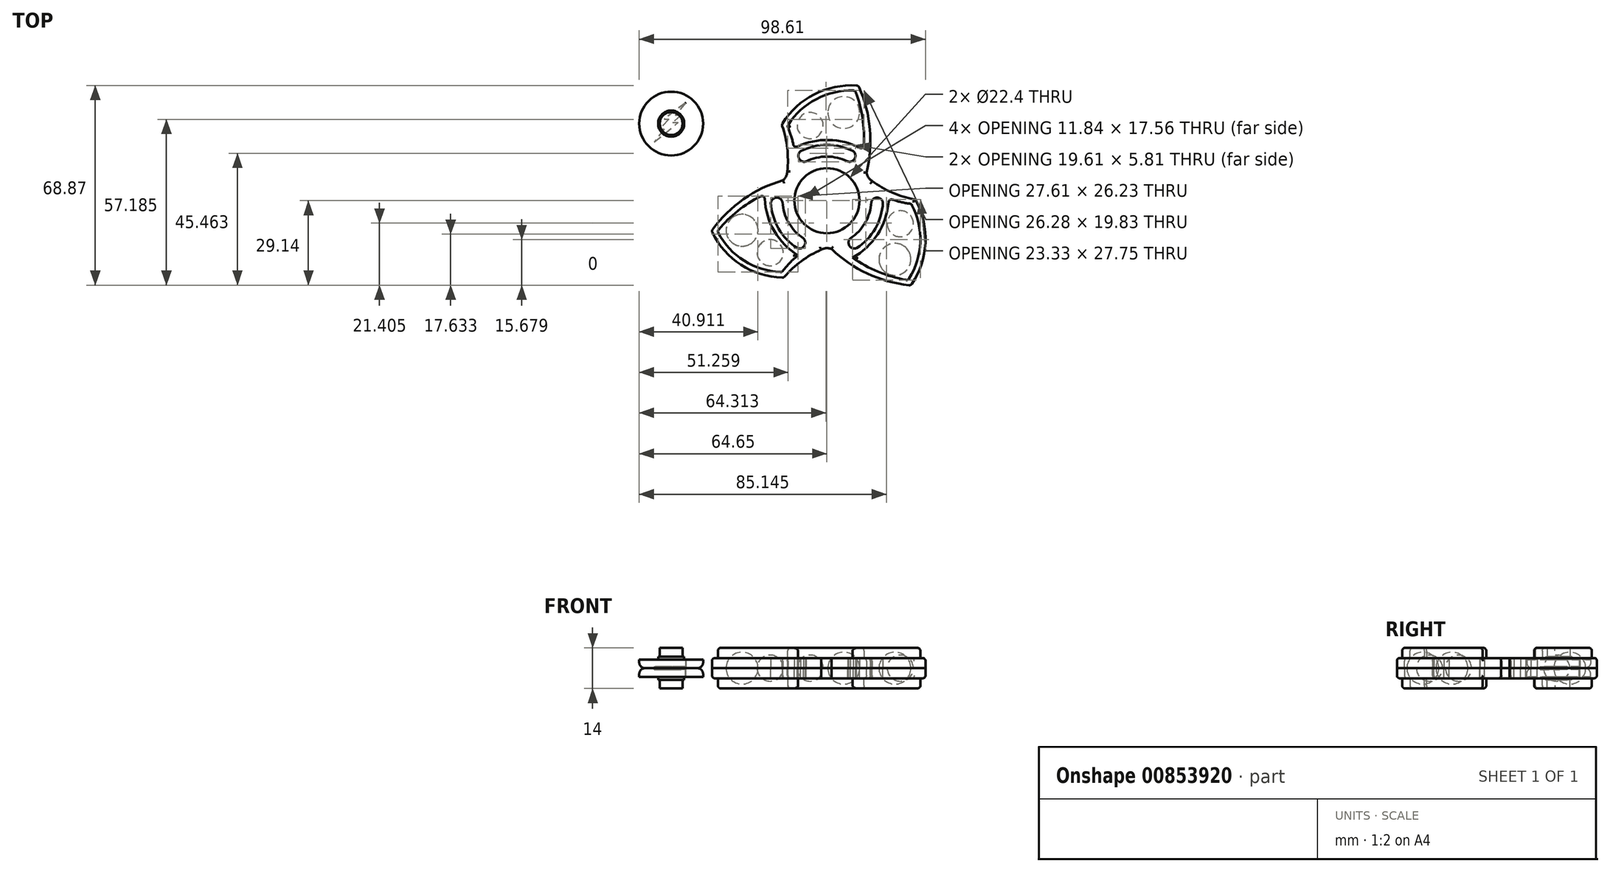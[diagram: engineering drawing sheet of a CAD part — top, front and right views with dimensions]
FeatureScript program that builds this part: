
annotation { "Feature Type Name" : "Feature", "Feature Type Description" : "" }
export const myFeature = defineFeature(function(context is Context, id is Id, definition is map)
    precondition{}
    {
        {
            var Q0;
            Q0=qCreatedBy(makeId("Top.planeOp"),FACE);
            var sketch = newSketch(context, id + "F0", { "sketchPlane" : qUnion([Q0])});
            skCircle(sketch, "E0", {"center": v(0, 0) * mm, "radius": 13.7 * mm});
            skCircle(sketch, "E1", {"center": v(0, 0) * mm, "radius": 11.2 * mm});
            skCircle(sketch, "E2", {"center": v(-53.65, 26.57) * mm, "radius": 11 * mm});
            skCircle(sketch, "E3", {"center": v(-53.65, 26.57) * mm, "radius": 3.95 * mm});
            skCircle(sketch, "E4", {"center": v(-53.65, 26.57) * mm, "radius": 6.92 * mm});
            skCircle(sketch, "E5", {"center": v(-53.65, 26.57) * mm, "radius": 8.68 * mm});
            skPoint(sketch, "E6.MirrorP", {"position": v(9.06, 17.07) * mm});
            skPoint(sketch, "E7.MirrorP", {"position": v(7.21, 13.5) * mm});
            skPoint(sketch, "E8", {"position": v(0, 15.2) * mm});
            skPoint(sketch, "E9", {"position": v(0, 19.23) * mm});
            skArc(sketch, "E10", {"start": v(7.21, 13.5) * mm, "mid": v(0, 15.2) * mm, "end": v(-7.21, 13.5) * mm});
            skArc(sketch, "E11", {"start": v(9.06, 17.07) * mm, "mid": v(0, 19.23) * mm, "end": v(-9.06, 17.07) * mm});
            skArc(sketch, "E12", {"start": v(-9.06, 17.07) * mm, "mid": v(-9.6, 14.52) * mm, "end": v(-7.21, 13.5) * mm});
            skArc(sketch, "E13.MirrorCS", {"start": v(9.06, 17.07) * mm, "mid": v(9.6, 14.52) * mm, "end": v(7.21, 13.5) * mm});
            skPoint(sketch, "E14", {"position": v(0, 20.93) * mm});
            skArc(sketch, "E15", {"start": v(12.63, 17.5) * mm, "mid": v(0.7, 20.92) * mm, "end": v(-11.37, 18.03) * mm});
            skCircle(sketch, "E16.MirrorC", {"center": v(-5.77, 25.88) * mm, "radius": 4.5 * mm});
            skLineSegment(sketch, "E17", {"start": v(0.3, 30.4) * mm, "end": v(11.3, 30.4) * mm});
            skCircle(sketch, "E18", {"center": v(5.8, 30.4) * mm, "radius": 5.5 * mm});
            skLineSegment(sketch, "E19", {"start": v(-1.27, 25.88) * mm, "end": v(-10.27, 25.88) * mm});
            skArc(sketch, "E20", {"start": v(-11.37, 18.03) * mm, "mid": v(-12.22, 21.95) * mm, "end": v(-13.6, 25.71) * mm});
            skArc(sketch, "E21", {"start": v(12.63, 17.5) * mm, "mid": v(12.36, 27.87) * mm, "end": v(9.77, 37.93) * mm});
            skArc(sketch, "E22", {"start": v(9.77, 37.93) * mm, "mid": v(-3.6, 35.05) * mm, "end": v(-13.6, 25.71) * mm});
            skPoint(sketch, "E23", {"position": v(12.8, 22.5) * mm});
            skPoint(sketch, "E24", {"position": v(-15.55, 26.2) * mm});
            skPoint(sketch, "E25", {"position": v(10.84, 39.63) * mm});
            skPoint(sketch, "E26", {"position": v(13.64, 9.66) * mm});
            skPoint(sketch, "E27", {"position": v(-13.65, 10.14) * mm});
            skArc(sketch, "E28", {"start": v(10.84, 39.63) * mm, "mid": v(-4.28, 36.7) * mm, "end": v(-15.55, 26.2) * mm});
            skArc(sketch, "E29", {"start": v(13.64, 9.66) * mm, "mid": v(14.79, 24.88) * mm, "end": v(10.84, 39.63) * mm});
            skPoint(sketch, "E30", {"position": v(14.97, 19.42) * mm});
            skPoint(sketch, "E31", {"position": v(14.46, 27.55) * mm});
            skArc(sketch, "E32", {"start": v(-13.65, 10.14) * mm, "mid": v(-13.69, 18.28) * mm, "end": v(-15.55, 26.2) * mm});
            skPoint(sketch, "E33.1.0", {"position": v(-13.16, -7.6) * mm});
            skArc(sketch, "E33.1.1", {"start": v(-21.47, 2.2) * mm, "mid": v(-18.47, -9.85) * mm, "end": v(-9.93, -18.86) * mm});
            skCircle(sketch, "E33.1.2", {"center": v(-29.22, -10.18) * mm, "radius": 5.5 * mm});
            skArc(sketch, "E33.1.3", {"start": v(-19.31, -0.69) * mm, "mid": v(-16.65, -9.61) * mm, "end": v(-10.25, -16.38) * mm});
            skArc(sketch, "E33.1.4", {"start": v(-15.29, -0.5) * mm, "mid": v(-13.16, -7.6) * mm, "end": v(-8.08, -13) * mm});
            skPoint(sketch, "E33.1.5", {"position": v(-25.89, -0.17) * mm});
            skArc(sketch, "E33.1.6", {"start": v(-21.47, 2.2) * mm, "mid": v(-30.32, -3.23) * mm, "end": v(-37.74, -10.5) * mm});
            skLineSegment(sketch, "E33.1.7", {"start": v(-26.47, -14.95) * mm, "end": v(-31.97, -5.42) * mm});
            skPoint(sketch, "E33.1.8", {"position": v(-16.65, -9.61) * mm});
            skPoint(sketch, "E33.1.9", {"position": v(-15.29, -0.5) * mm});
            skPoint(sketch, "E33.1.10", {"position": v(-18.12, -10.46) * mm});
            skArc(sketch, "E33.1.11", {"start": v(-9.93, -18.86) * mm, "mid": v(-12.9, -21.56) * mm, "end": v(-15.46, -24.64) * mm});
            skPoint(sketch, "E33.1.12", {"position": v(-39.74, -10.43) * mm});
            skPoint(sketch, "E33.1.13", {"position": v(-24.3, 3.25) * mm});
            skPoint(sketch, "E33.1.14", {"position": v(-14.92, -26.57) * mm});
            skPoint(sketch, "E33.1.15", {"position": v(-15.19, 6.98) * mm});
            skPoint(sketch, "E33.1.16", {"position": v(-19.31, -0.69) * mm});
            skLineSegment(sketch, "E33.1.17", {"start": v(-21.78, -14.04) * mm, "end": v(-17.28, -21.83) * mm});
            skPoint(sketch, "E33.1.18", {"position": v(-31.1, -1.26) * mm});
            skArc(sketch, "E33.1.19", {"start": v(-39.74, -10.43) * mm, "mid": v(-29.64, -22.06) * mm, "end": v(-14.92, -26.57) * mm});
            skArc(sketch, "E33.1.20", {"start": v(-19.31, -0.69) * mm, "mid": v(-17.38, 1.05) * mm, "end": v(-15.29, -0.5) * mm});
            skArc(sketch, "E33.1.21", {"start": v(-37.74, -10.5) * mm, "mid": v(-28.55, -20.65) * mm, "end": v(-15.46, -24.64) * mm});
            skArc(sketch, "E33.1.22", {"start": v(-10.25, -16.38) * mm, "mid": v(-7.78, -15.57) * mm, "end": v(-8.08, -13) * mm});
            skCircle(sketch, "E33.1.23", {"center": v(-19.53, -17.93) * mm, "radius": 4.5 * mm});
            skArc(sketch, "E33.1.24", {"start": v(-15.19, 6.98) * mm, "mid": v(-28.94, 0.36) * mm, "end": v(-39.74, -10.43) * mm});
            skArc(sketch, "E33.1.25", {"start": v(-1.96, -16.89) * mm, "mid": v(-8.99, -21) * mm, "end": v(-14.92, -26.57) * mm});
            skPoint(sketch, "E33.2.0", {"position": v(13.16, -7.6) * mm});
            skArc(sketch, "E33.2.1", {"start": v(8.83, -19.69) * mm, "mid": v(17.77, -11.07) * mm, "end": v(21.3, 0.83) * mm});
            skCircle(sketch, "E33.2.2", {"center": v(23.43, -20.21) * mm, "radius": 5.5 * mm});
            skArc(sketch, "E33.2.3", {"start": v(10.25, -16.38) * mm, "mid": v(16.65, -9.61) * mm, "end": v(19.31, -0.69) * mm});
            skArc(sketch, "E33.2.4", {"start": v(8.08, -13) * mm, "mid": v(13.16, -7.6) * mm, "end": v(15.29, -0.5) * mm});
            skPoint(sketch, "E33.2.5", {"position": v(13.1, -22.33) * mm});
            skArc(sketch, "E33.2.6", {"start": v(8.83, -19.69) * mm, "mid": v(17.96, -24.64) * mm, "end": v(27.96, -27.43) * mm});
            skLineSegment(sketch, "E33.2.7", {"start": v(26.18, -15.45) * mm, "end": v(20.68, -24.98) * mm});
            skPoint(sketch, "E33.2.8", {"position": v(16.65, -9.61) * mm});
            skPoint(sketch, "E33.2.9", {"position": v(8.08, -13) * mm});
            skPoint(sketch, "E33.2.10", {"position": v(18.12, -10.46) * mm});
            skArc(sketch, "E33.2.11", {"start": v(21.3, 0.83) * mm, "mid": v(25.12, -0.4) * mm, "end": v(29.07, -1.07) * mm});
            skPoint(sketch, "E33.2.12", {"position": v(28.9, -29.2) * mm});
            skPoint(sketch, "E33.2.13", {"position": v(9.33, -22.67) * mm});
            skPoint(sketch, "E33.2.14", {"position": v(30.47, 0.36) * mm});
            skPoint(sketch, "E33.2.15", {"position": v(1.55, -16.65) * mm});
            skPoint(sketch, "E33.2.16", {"position": v(10.25, -16.38) * mm});
            skLineSegment(sketch, "E33.2.17", {"start": v(23.04, -11.84) * mm, "end": v(27.54, -4.05) * mm});
            skPoint(sketch, "E33.2.18", {"position": v(16.63, -26.3) * mm});
            skArc(sketch, "E33.2.19", {"start": v(28.9, -29.2) * mm, "mid": v(33.92, -14.64) * mm, "end": v(30.47, 0.36) * mm});
            skArc(sketch, "E33.2.20", {"start": v(10.25, -16.38) * mm, "mid": v(7.78, -15.57) * mm, "end": v(8.08, -13) * mm});
            skArc(sketch, "E33.2.21", {"start": v(27.96, -27.43) * mm, "mid": v(32.16, -14.4) * mm, "end": v(29.07, -1.07) * mm});
            skArc(sketch, "E33.2.22", {"start": v(19.31, -0.69) * mm, "mid": v(17.38, 1.05) * mm, "end": v(15.29, -0.5) * mm});
            skCircle(sketch, "E33.2.23", {"center": v(25.3, -7.95) * mm, "radius": 4.5 * mm});
            skArc(sketch, "E33.2.24", {"start": v(1.55, -16.65) * mm, "mid": v(14.16, -25.25) * mm, "end": v(28.9, -29.2) * mm});
            skArc(sketch, "E33.2.25", {"start": v(15.6, 6.75) * mm, "mid": v(22.67, 2.71) * mm, "end": v(30.47, 0.36) * mm});
            skArc(sketch, "E34", {"start": v(-15.19, 6.98) * mm, "mid": v(-14.07, 8.4) * mm, "end": v(-13.65, 10.14) * mm});
            skArc(sketch, "E35.1.0", {"start": v(1.55, -16.65) * mm, "mid": v(-0.23, -16.38) * mm, "end": v(-1.96, -16.89) * mm});
            skArc(sketch, "E35.2.0", {"start": v(13.64, 9.66) * mm, "mid": v(14.3, 7.99) * mm, "end": v(15.6, 6.75) * mm});
            skCircle(sketch, "E36", {"center": v(-53.65, 26.57) * mm, "radius": 4.5 * mm});
            skLineSegment(sketch, "E37", {"start": v(-48.56, 33.87) * mm, "end": v(-56.1, 28.05) * mm});
            skLineSegment(sketch, "E38", {"start": v(-56.1, 28.05) * mm, "end": v(-54.44, 28.05) * mm});
            skLineSegment(sketch, "E39", {"start": v(-54.44, 28.05) * mm, "end": v(-57.71, 24.64) * mm});
            skLineSegment(sketch, "E40", {"start": v(-57.71, 24.64) * mm, "end": v(-56.1, 24.64) * mm});
            skLineSegment(sketch, "E41", {"start": v(-56.1, 24.64) * mm, "end": v(-59.52, 20.18) * mm});
            skLineSegment(sketch, "E42", {"start": v(-59.52, 20.18) * mm, "end": v(-51.2, 26.98) * mm});
            skLineSegment(sketch, "E43", {"start": v(-48.56, 33.87) * mm, "end": v(-52.2, 29.55) * mm});
            skLineSegment(sketch, "E44", {"start": v(-52.2, 29.55) * mm, "end": v(-50.27, 29.55) * mm});
            skLineSegment(sketch, "E45", {"start": v(-50.27, 29.55) * mm, "end": v(-53.14, 26.91) * mm});
            skLineSegment(sketch, "E46", {"start": v(-53.14, 26.91) * mm, "end": v(-51.2, 26.98) * mm});
            skSolve(sketch);
        }
        {
            var Q0;
            Q0=makeQuery(id+"F0.imprint","IMPRINT",FACE,{"disambiguationData":[TD([[makeQuery(id+"F0.imprint","IMPRINT",EDGE,{"derivedFrom":sQuery(id+"F0.wireOp",EDGE,"E0")}),-1.0]])]});
            var Q1;
            Q1=makeQuery(id+"F0.imprint","IMPRINT",FACE,{"disambiguationData":[TD([[makeQuery(id+"F0.imprint","IMPRINT",EDGE,{"derivedFrom":sQuery(id+"F0.wireOp",EDGE,"E33.2.1")}),-1.0]])]});
            var Q2;
            {var subQ0=sQuery(id+"F0.wireOp",EDGE,"E33.2.17");Q2=makeQuery(id+"F0.imprint","IMPRINT",FACE,{"disambiguationData":[TD([[makeQuery(id+"F0.imprint","IMPRINT",EDGE,{"derivedFrom":subQ0}),-1.0]])]});}
            var Q3;
            {var subQ0=sQuery(id+"F0.wireOp",EDGE,"E33.2.17");Q3=makeQuery(id+"F0.imprint","IMPRINT",FACE,{"disambiguationData":[TD([[makeQuery(id+"F0.imprint","IMPRINT",EDGE,{"derivedFrom":subQ0}),1.0]])]});}
            var Q4;
            {var subQ0=sQuery(id+"F0.wireOp",EDGE,"E33.2.7");Q4=makeQuery(id+"F0.imprint","IMPRINT",FACE,{"disambiguationData":[TD([[makeQuery(id+"F0.imprint","IMPRINT",EDGE,{"derivedFrom":subQ0}),-1.0]])]});}
            var Q5;
            {var subQ0=sQuery(id+"F0.wireOp",EDGE,"E33.2.7");Q5=makeQuery(id+"F0.imprint","IMPRINT",FACE,{"disambiguationData":[TD([[makeQuery(id+"F0.imprint","IMPRINT",EDGE,{"derivedFrom":subQ0}),1.0]])]});}
            var Q6;
            Q6=makeQuery(id+"F0.imprint","IMPRINT",FACE,{"disambiguationData":[TD([[makeQuery(id+"F0.imprint","IMPRINT",EDGE,{"derivedFrom":sQuery(id+"F0.wireOp",EDGE,"E33.1.1")}),-1.0]])]});
            var Q7;
            {var subQ0=sQuery(id+"F0.wireOp",EDGE,"E33.1.17");Q7=makeQuery(id+"F0.imprint","IMPRINT",FACE,{"disambiguationData":[TD([[makeQuery(id+"F0.imprint","IMPRINT",EDGE,{"derivedFrom":subQ0}),1.0]])]});}
            var Q8;
            {var subQ0=sQuery(id+"F0.wireOp",EDGE,"E33.1.17");Q8=makeQuery(id+"F0.imprint","IMPRINT",FACE,{"disambiguationData":[TD([[makeQuery(id+"F0.imprint","IMPRINT",EDGE,{"derivedFrom":subQ0}),-1.0]])]});}
            var Q9;
            {var subQ0=sQuery(id+"F0.wireOp",EDGE,"E33.1.7");Q9=makeQuery(id+"F0.imprint","IMPRINT",FACE,{"disambiguationData":[TD([[makeQuery(id+"F0.imprint","IMPRINT",EDGE,{"derivedFrom":subQ0}),-1.0]])]});}
            var Q10;
            {var subQ0=sQuery(id+"F0.wireOp",EDGE,"E33.1.7");Q10=makeQuery(id+"F0.imprint","IMPRINT",FACE,{"disambiguationData":[TD([[makeQuery(id+"F0.imprint","IMPRINT",EDGE,{"derivedFrom":subQ0}),1.0]])]});}
            var Q11;
            Q11=makeQuery(id+"F0.imprint","IMPRINT",FACE,{"disambiguationData":[TD([[makeQuery(id+"F0.imprint","IMPRINT",EDGE,{"derivedFrom":sQuery(id+"F0.wireOp",EDGE,"E15")}),-1.0]])]});
            var Q12;
            {var subQ0=sQuery(id+"F0.wireOp",EDGE,"E17");Q12=makeQuery(id+"F0.imprint","IMPRINT",FACE,{"disambiguationData":[TD([[makeQuery(id+"F0.imprint","IMPRINT",EDGE,{"derivedFrom":subQ0}),-1.0]])]});}
            var Q13;
            {var subQ0=sQuery(id+"F0.wireOp",EDGE,"E17");Q13=makeQuery(id+"F0.imprint","IMPRINT",FACE,{"disambiguationData":[TD([[makeQuery(id+"F0.imprint","IMPRINT",EDGE,{"derivedFrom":subQ0}),1.0]])]});}
            var Q14;
            {var subQ0=sQuery(id+"F0.wireOp",EDGE,"E19");Q14=makeQuery(id+"F0.imprint","IMPRINT",FACE,{"disambiguationData":[TD([[makeQuery(id+"F0.imprint","IMPRINT",EDGE,{"derivedFrom":subQ0}),-1.0]])]});}
            var Q15;
            {var subQ0=sQuery(id+"F0.wireOp",EDGE,"E19");Q15=makeQuery(id+"F0.imprint","IMPRINT",FACE,{"disambiguationData":[TD([[makeQuery(id+"F0.imprint","IMPRINT",EDGE,{"derivedFrom":subQ0}),1.0]])]});}
            var Q16;
            Q16=makeQuery(id+"F0.imprint","IMPRINT",FACE,{"disambiguationData":[TD([[makeQuery(id+"F0.imprint","IMPRINT",EDGE,{"derivedFrom":sQuery(id+"F0.wireOp",EDGE,"E0")}),1.0]])]});
            extrude(context, id + "F1", {"entities" : qUnion([Q0, Q1, Q2, Q3, Q4, Q5, Q6, Q7, Q8, Q9, Q10, Q11, Q12, Q13, Q14, Q15, Q16]), "depth" : 3.5 * mm, "offsetDistance" : 25 * mm});
        }
        {
            var Q0;
            Q0=makeQuery(id+"F0.imprint","IMPRINT",FACE,{"disambiguationData":[TD([[makeQuery(id+"F0.imprint","IMPRINT",EDGE,{"derivedFrom":sQuery(id+"F0.wireOp",EDGE,"E15")}),-1.0]])]});
            var Q1;
            Q1=makeQuery(id+"F0.imprint","IMPRINT",FACE,{"disambiguationData":[TD([[makeQuery(id+"F0.imprint","IMPRINT",EDGE,{"derivedFrom":sQuery(id+"F0.wireOp",EDGE,"E33.1.1")}),-1.0]])]});
            var Q2;
            Q2=makeQuery(id+"F0.imprint","IMPRINT",FACE,{"disambiguationData":[TD([[makeQuery(id+"F0.imprint","IMPRINT",EDGE,{"derivedFrom":sQuery(id+"F0.wireOp",EDGE,"E33.2.1")}),-1.0]])]});
            var Q3;
            {var subQ0=sQuery(id+"F0.wireOp",EDGE,"E33.1.7");Q3=makeQuery(id+"F0.imprint","IMPRINT",FACE,{"disambiguationData":[TD([[makeQuery(id+"F0.imprint","IMPRINT",EDGE,{"derivedFrom":subQ0}),1.0]])]});}
            var Q4;
            {var subQ0=sQuery(id+"F0.wireOp",EDGE,"E33.1.7");Q4=makeQuery(id+"F0.imprint","IMPRINT",FACE,{"disambiguationData":[TD([[makeQuery(id+"F0.imprint","IMPRINT",EDGE,{"derivedFrom":subQ0}),-1.0]])]});}
            var Q5;
            {var subQ0=sQuery(id+"F0.wireOp",EDGE,"E33.1.17");Q5=makeQuery(id+"F0.imprint","IMPRINT",FACE,{"disambiguationData":[TD([[makeQuery(id+"F0.imprint","IMPRINT",EDGE,{"derivedFrom":subQ0}),-1.0]])]});}
            var Q6;
            {var subQ0=sQuery(id+"F0.wireOp",EDGE,"E33.1.17");Q6=makeQuery(id+"F0.imprint","IMPRINT",FACE,{"disambiguationData":[TD([[makeQuery(id+"F0.imprint","IMPRINT",EDGE,{"derivedFrom":subQ0}),1.0]])]});}
            var Q7;
            {var subQ0=sQuery(id+"F0.wireOp",EDGE,"E19");Q7=makeQuery(id+"F0.imprint","IMPRINT",FACE,{"disambiguationData":[TD([[makeQuery(id+"F0.imprint","IMPRINT",EDGE,{"derivedFrom":subQ0}),1.0]])]});}
            var Q8;
            {var subQ0=sQuery(id+"F0.wireOp",EDGE,"E19");Q8=makeQuery(id+"F0.imprint","IMPRINT",FACE,{"disambiguationData":[TD([[makeQuery(id+"F0.imprint","IMPRINT",EDGE,{"derivedFrom":subQ0}),-1.0]])]});}
            var Q9;
            {var subQ0=sQuery(id+"F0.wireOp",EDGE,"E17");Q9=makeQuery(id+"F0.imprint","IMPRINT",FACE,{"disambiguationData":[TD([[makeQuery(id+"F0.imprint","IMPRINT",EDGE,{"derivedFrom":subQ0}),-1.0]])]});}
            var Q10;
            {var subQ0=sQuery(id+"F0.wireOp",EDGE,"E17");Q10=makeQuery(id+"F0.imprint","IMPRINT",FACE,{"disambiguationData":[TD([[makeQuery(id+"F0.imprint","IMPRINT",EDGE,{"derivedFrom":subQ0}),1.0]])]});}
            var Q11;
            {var subQ0=sQuery(id+"F0.wireOp",EDGE,"E33.2.17");Q11=makeQuery(id+"F0.imprint","IMPRINT",FACE,{"disambiguationData":[TD([[makeQuery(id+"F0.imprint","IMPRINT",EDGE,{"derivedFrom":subQ0}),1.0]])]});}
            var Q12;
            {var subQ0=sQuery(id+"F0.wireOp",EDGE,"E33.2.17");Q12=makeQuery(id+"F0.imprint","IMPRINT",FACE,{"disambiguationData":[TD([[makeQuery(id+"F0.imprint","IMPRINT",EDGE,{"derivedFrom":subQ0}),-1.0]])]});}
            var Q13;
            {var subQ0=sQuery(id+"F0.wireOp",EDGE,"E33.2.7");Q13=makeQuery(id+"F0.imprint","IMPRINT",FACE,{"disambiguationData":[TD([[makeQuery(id+"F0.imprint","IMPRINT",EDGE,{"derivedFrom":subQ0}),-1.0]])]});}
            var Q14;
            {var subQ0=sQuery(id+"F0.wireOp",EDGE,"E33.2.7");Q14=makeQuery(id+"F0.imprint","IMPRINT",FACE,{"disambiguationData":[TD([[makeQuery(id+"F0.imprint","IMPRINT",EDGE,{"derivedFrom":subQ0}),1.0]])]});}
            extrude(context, id + "F2", {"entities" : qUnion([Q0, Q1, Q2, Q3, Q4, Q5, Q6, Q7, Q8, Q9, Q10, Q11, Q12, Q13, Q14]), "operationType" : NewBodyOperationType.ADD, "depth" : 7 * mm, "offsetDistance" : 25 * mm});
        }
        {
            var Q0;
            Q0=makeQuery(id+"F2.opExtrude","CAP_EDGE",EDGE,{"disambiguationData":[OSD([sQuery(id+"F0.wireOp",EDGE,"E20")])],"isStart":false});
            var Q1;
            Q1=makeQuery(id+"F2.opExtrude","CAP_EDGE",EDGE,{"disambiguationData":[OSD([sQuery(id+"F0.wireOp",EDGE,"E22")])],"isStart":false});
            var Q2;
            Q2=makeQuery(id+"F2.opExtrude","CAP_EDGE",EDGE,{"disambiguationData":[OSD([sQuery(id+"F0.wireOp",EDGE,"E15")])],"isStart":false});
            var Q3;
            Q3=makeQuery(id+"F2.opExtrude","CAP_EDGE",EDGE,{"disambiguationData":[OSD([sQuery(id+"F0.wireOp",EDGE,"E21")])],"isStart":false});
            var Q4;
            Q4=makeQuery(id+"F1.opExtrude","CAP_EDGE",EDGE,{"disambiguationData":[OSD([sQuery(id+"F0.wireOp",EDGE,"E28")])],"isStart":false});
            var Q5;
            Q5=makeQuery(id+"F1.opExtrude","CAP_EDGE",EDGE,{"disambiguationData":[OSD([sQuery(id+"F0.wireOp",EDGE,"E29")])],"isStart":false});
            var Q6;
            Q6=makeQuery(id+"F1.opExtrude","CAP_EDGE",EDGE,{"disambiguationData":[OSD([sQuery(id+"F0.wireOp",EDGE,"E32")])],"isStart":false});
            var Q7;
            Q7=makeQuery(id+"F1.opExtrude","CAP_EDGE",EDGE,{"disambiguationData":[OSD([sQuery(id+"F0.wireOp",EDGE,"E34")])],"isStart":false});
            var Q8;
            Q8=makeQuery(id+"F1.opExtrude","CAP_EDGE",EDGE,{"disambiguationData":[OSD([sQuery(id+"F0.wireOp",EDGE,"E35.2.0")])],"isStart":false});
            var Q9;
            Q9=makeQuery(id+"F1.opExtrude","CAP_EDGE",EDGE,{"disambiguationData":[OSD([sQuery(id+"F0.wireOp",EDGE,"E33.1.24")])],"isStart":false});
            var Q10;
            Q10=makeQuery(id+"F1.opExtrude","CAP_EDGE",EDGE,{"disambiguationData":[OSD([sQuery(id+"F0.wireOp",EDGE,"E33.1.19")])],"isStart":false});
            var Q11;
            Q11=makeQuery(id+"F2.opExtrude","CAP_EDGE",EDGE,{"disambiguationData":[OSD([sQuery(id+"F0.wireOp",EDGE,"E33.1.21")])],"isStart":false});
            var Q12;
            Q12=makeQuery(id+"F2.opExtrude","CAP_EDGE",EDGE,{"disambiguationData":[OSD([sQuery(id+"F0.wireOp",EDGE,"E33.1.6")])],"isStart":false});
            var Q13;
            Q13=makeQuery(id+"F2.opExtrude","CAP_EDGE",EDGE,{"disambiguationData":[OSD([sQuery(id+"F0.wireOp",EDGE,"E33.1.1")])],"isStart":false});
            var Q14;
            Q14=makeQuery(id+"F2.opExtrude","CAP_EDGE",EDGE,{"disambiguationData":[OSD([sQuery(id+"F0.wireOp",EDGE,"E33.1.11")])],"isStart":false});
            var Q15;
            Q15=makeQuery(id+"F1.opExtrude","CAP_EDGE",EDGE,{"disambiguationData":[OSD([sQuery(id+"F0.wireOp",EDGE,"E33.1.25")])],"isStart":false});
            var Q16;
            Q16=makeQuery(id+"F1.opExtrude","SWEPT_EDGE",EDGE,{"disambiguationData":[OSD([sQuery(id+"F0.wireOp",EDGE,"E33.1.19"),sQuery(id+"F0.wireOp",EDGE,"E33.1.25")])]});
            var Q17;
            Q17=makeQuery(id+"F2.opExtrude","SWEPT_EDGE",EDGE,{"disambiguationData":[OSD([sQuery(id+"F0.wireOp",EDGE,"E33.1.11"),sQuery(id+"F0.wireOp",EDGE,"E33.1.21")])]});
            var Q18;
            Q18=makeQuery(id+"F2.opExtrude","SWEPT_EDGE",EDGE,{"disambiguationData":[OSD([sQuery(id+"F0.wireOp",EDGE,"E33.1.1"),sQuery(id+"F0.wireOp",EDGE,"E33.1.6")])]});
            var Q19;
            Q19=makeQuery(id+"F2.opExtrude","SWEPT_EDGE",EDGE,{"disambiguationData":[OSD([sQuery(id+"F0.wireOp",EDGE,"E33.1.6"),sQuery(id+"F0.wireOp",EDGE,"E33.1.21")])]});
            var Q20;
            Q20=makeQuery(id+"F1.opExtrude","SWEPT_EDGE",EDGE,{"disambiguationData":[OSD([sQuery(id+"F0.wireOp",EDGE,"E33.1.19"),sQuery(id+"F0.wireOp",EDGE,"E33.1.24")])]});
            var Q21;
            Q21=makeQuery(id+"F1.opExtrude","CAP_EDGE",EDGE,{"disambiguationData":[OSD([sQuery(id+"F0.wireOp",EDGE,"E33.2.25")])],"isStart":false});
            var Q22;
            Q22=makeQuery(id+"F1.opExtrude","CAP_EDGE",EDGE,{"disambiguationData":[OSD([sQuery(id+"F0.wireOp",EDGE,"E33.2.24")])],"isStart":false});
            var Q23;
            Q23=makeQuery(id+"F1.opExtrude","CAP_EDGE",EDGE,{"disambiguationData":[OSD([sQuery(id+"F0.wireOp",EDGE,"E35.1.0")])],"isStart":false});
            var Q24;
            Q24=makeQuery(id+"F1.opExtrude","SWEPT_EDGE",EDGE,{"disambiguationData":[OSD([sQuery(id+"F0.wireOp",EDGE,"E33.2.19"),sQuery(id+"F0.wireOp",EDGE,"E33.2.24")])]});
            var Q25;
            Q25=makeQuery(id+"F2.opExtrude","SWEPT_EDGE",EDGE,{"disambiguationData":[OSD([sQuery(id+"F0.wireOp",EDGE,"E33.2.6"),sQuery(id+"F0.wireOp",EDGE,"E33.2.21")])]});
            var Q26;
            Q26=makeQuery(id+"F2.opExtrude","CAP_EDGE",EDGE,{"disambiguationData":[OSD([sQuery(id+"F0.wireOp",EDGE,"E33.2.6")])],"isStart":false});
            var Q27;
            Q27=makeQuery(id+"F2.opExtrude","CAP_EDGE",EDGE,{"disambiguationData":[OSD([sQuery(id+"F0.wireOp",EDGE,"E33.2.21")])],"isStart":false});
            var Q28;
            Q28=makeQuery(id+"F2.opExtrude","CAP_EDGE",EDGE,{"disambiguationData":[OSD([sQuery(id+"F0.wireOp",EDGE,"E33.2.1")])],"isStart":false});
            var Q29;
            Q29=makeQuery(id+"F1.opExtrude","CAP_EDGE",EDGE,{"disambiguationData":[OSD([sQuery(id+"F0.wireOp",EDGE,"E33.2.19")])],"isStart":false});
            var Q30;
            Q30=makeQuery(id+"F1.opExtrude","SWEPT_EDGE",EDGE,{"disambiguationData":[OSD([sQuery(id+"F0.wireOp",EDGE,"E33.2.19"),sQuery(id+"F0.wireOp",EDGE,"E33.2.25")])]});
            var Q31;
            Q31=makeQuery(id+"F2.opExtrude","SWEPT_EDGE",EDGE,{"disambiguationData":[OSD([sQuery(id+"F0.wireOp",EDGE,"E33.2.11"),sQuery(id+"F0.wireOp",EDGE,"E33.2.21")])]});
            var Q32;
            Q32=makeQuery(id+"F2.opExtrude","SWEPT_EDGE",EDGE,{"disambiguationData":[OSD([sQuery(id+"F0.wireOp",EDGE,"E33.2.1"),sQuery(id+"F0.wireOp",EDGE,"E33.2.11")])]});
            var Q33;
            Q33=makeQuery(id+"F2.opExtrude","CAP_EDGE",EDGE,{"disambiguationData":[OSD([sQuery(id+"F0.wireOp",EDGE,"E33.2.11")])],"isStart":false});
            var Q34;
            Q34=makeQuery(id+"F1.opExtrude","SWEPT_EDGE",EDGE,{"disambiguationData":[OSD([sQuery(id+"F0.wireOp",EDGE,"E28"),sQuery(id+"F0.wireOp",EDGE,"E29")])]});
            var Q35;
            Q35=makeQuery(id+"F2.opExtrude","SWEPT_EDGE",EDGE,{"disambiguationData":[OSD([sQuery(id+"F0.wireOp",EDGE,"E21"),sQuery(id+"F0.wireOp",EDGE,"E22")])]});
            var Q36;
            Q36=makeQuery(id+"F1.opExtrude","SWEPT_EDGE",EDGE,{"disambiguationData":[OSD([sQuery(id+"F0.wireOp",EDGE,"E28"),sQuery(id+"F0.wireOp",EDGE,"E32")])]});
            var Q37;
            Q37=makeQuery(id+"F2.opExtrude","SWEPT_EDGE",EDGE,{"disambiguationData":[OSD([sQuery(id+"F0.wireOp",EDGE,"E20"),sQuery(id+"F0.wireOp",EDGE,"E22")])]});
            var Q38;
            Q38=makeQuery(id+"F2.opExtrude","SWEPT_EDGE",EDGE,{"disambiguationData":[OSD([sQuery(id+"F0.wireOp",EDGE,"E15"),sQuery(id+"F0.wireOp",EDGE,"E20")])]});
            var Q39;
            Q39=makeQuery(id+"F2.opExtrude","SWEPT_EDGE",EDGE,{"disambiguationData":[OSD([sQuery(id+"F0.wireOp",EDGE,"E15"),sQuery(id+"F0.wireOp",EDGE,"E21")])]});
            fillet(context, id + "F3", {"entities" : qUnion([Q0, Q1, Q2, Q3, Q4, Q5, Q6, Q7, Q8, Q9, Q10, Q11, Q12, Q13, Q14, Q15, Q16, Q17, Q18, Q19, Q20, Q21, Q22, Q23, Q24, Q25, Q26, Q27, Q28, Q29, Q30, Q31, Q32, Q33, Q34, Q35, Q36, Q37, Q38, Q39]), "radius" : 1 * mm, "tangentPropagation" : true, "allowEdgeOverflow" : false});
        }
        {
            var Q0;
            Q0=makeQuery(id+"F1.opExtrude","SWEPT_BODY",BODY,{"disambiguationData":[OSD([sQuery(id+"F0.wireOp",EDGE,"E1"),sQuery(id+"F0.wireOp",EDGE,"E10"),sQuery(id+"F0.wireOp",EDGE,"E11"),sQuery(id+"F0.wireOp",EDGE,"E12"),sQuery(id+"F0.wireOp",EDGE,"E13.MirrorCS"),sQuery(id+"F0.wireOp",EDGE,"E28"),sQuery(id+"F0.wireOp",EDGE,"E29"),sQuery(id+"F0.wireOp",EDGE,"E32"),sQuery(id+"F0.wireOp",EDGE,"E33.1.3"),sQuery(id+"F0.wireOp",EDGE,"E33.1.4"),sQuery(id+"F0.wireOp",EDGE,"E33.1.19"),sQuery(id+"F0.wireOp",EDGE,"E33.1.20"),sQuery(id+"F0.wireOp",EDGE,"E33.1.22"),sQuery(id+"F0.wireOp",EDGE,"E33.1.24"),sQuery(id+"F0.wireOp",EDGE,"E33.1.25"),sQuery(id+"F0.wireOp",EDGE,"E33.2.3"),sQuery(id+"F0.wireOp",EDGE,"E33.2.4"),sQuery(id+"F0.wireOp",EDGE,"E33.2.19"),sQuery(id+"F0.wireOp",EDGE,"E33.2.20"),sQuery(id+"F0.wireOp",EDGE,"E33.2.22"),sQuery(id+"F0.wireOp",EDGE,"E33.2.24"),sQuery(id+"F0.wireOp",EDGE,"E33.2.25"),sQuery(id+"F0.wireOp",EDGE,"E34"),sQuery(id+"F0.wireOp",EDGE,"E35.1.0"),sQuery(id+"F0.wireOp",EDGE,"E35.2.0")])]});
            var Q1;
            Q1=qCreatedBy(makeId("Top.planeOp"),FACE);
            mirror(context, id + "F4", {"entities" : qUnion([Q0]), "mirrorPlane" : qUnion([Q1])});
        }
        {
            var Q0;
            {var subQ0=sQuery(id+"F0.wireOp",EDGE,"E19");Q0=makeQuery(id+"F0.imprint","IMPRINT",FACE,{"disambiguationData":[TD([[makeQuery(id+"F0.imprint","IMPRINT",EDGE,{"derivedFrom":subQ0}),1.0]])]});}
            var Q1;
            Q1=sQuery(id+"F0.wireOp",EDGE,"E19");
            revolve(context, id + "F5", {"operationType" : NewBodyOperationType.REMOVE, "surfaceOperationType" : NewSurfaceOperationType.NEW, "entities" : qUnion([Q0]), "axis" : qUnion([Q1]), "revolveType" : RevolveType.FULL, "oppositeDirection" : true});
        }
        {
            var Q0;
            {var subQ0=sQuery(id+"F0.wireOp",EDGE,"E17");Q0=makeQuery(id+"F0.imprint","IMPRINT",FACE,{"disambiguationData":[TD([[makeQuery(id+"F0.imprint","IMPRINT",EDGE,{"derivedFrom":subQ0}),1.0]])]});}
            var Q1;
            Q1=sQuery(id+"F0.wireOp",EDGE,"E17");
            revolve(context, id + "F6", {"operationType" : NewBodyOperationType.REMOVE, "surfaceOperationType" : NewSurfaceOperationType.NEW, "entities" : qUnion([Q0]), "axis" : qUnion([Q1]), "revolveType" : RevolveType.FULL, "oppositeDirection" : true});
        }
        {
            var Q0;
            {var subQ0=sQuery(id+"F0.wireOp",EDGE,"E33.1.7");Q0=makeQuery(id+"F0.imprint","IMPRINT",FACE,{"disambiguationData":[TD([[makeQuery(id+"F0.imprint","IMPRINT",EDGE,{"derivedFrom":subQ0}),1.0]])]});}
            var Q1;
            Q1=sQuery(id+"F0.wireOp",EDGE,"E33.1.7");
            revolve(context, id + "F7", {"operationType" : NewBodyOperationType.REMOVE, "surfaceOperationType" : NewSurfaceOperationType.NEW, "entities" : qUnion([Q0]), "axis" : qUnion([Q1]), "revolveType" : RevolveType.FULL, "oppositeDirection" : true});
        }
        {
            var Q0;
            {var subQ0=sQuery(id+"F0.wireOp",EDGE,"E33.1.17");Q0=makeQuery(id+"F0.imprint","IMPRINT",FACE,{"disambiguationData":[TD([[makeQuery(id+"F0.imprint","IMPRINT",EDGE,{"derivedFrom":subQ0}),-1.0]])]});}
            var Q1;
            Q1=sQuery(id+"F0.wireOp",EDGE,"E33.1.17");
            revolve(context, id + "F8", {"operationType" : NewBodyOperationType.REMOVE, "surfaceOperationType" : NewSurfaceOperationType.NEW, "entities" : qUnion([Q0]), "axis" : qUnion([Q1]), "revolveType" : RevolveType.FULL, "oppositeDirection" : true});
        }
        {
            var Q0;
            {var subQ0=sQuery(id+"F0.wireOp",EDGE,"E33.2.17");Q0=makeQuery(id+"F0.imprint","IMPRINT",FACE,{"disambiguationData":[TD([[makeQuery(id+"F0.imprint","IMPRINT",EDGE,{"derivedFrom":subQ0}),-1.0]])]});}
            var Q1;
            Q1=sQuery(id+"F0.wireOp",EDGE,"E33.2.17");
            revolve(context, id + "F9", {"operationType" : NewBodyOperationType.REMOVE, "surfaceOperationType" : NewSurfaceOperationType.NEW, "entities" : qUnion([Q0]), "axis" : qUnion([Q1]), "revolveType" : RevolveType.FULL, "oppositeDirection" : true});
        }
        {
            var Q0;
            {var subQ0=sQuery(id+"F0.wireOp",EDGE,"E33.2.7");Q0=makeQuery(id+"F0.imprint","IMPRINT",FACE,{"disambiguationData":[TD([[makeQuery(id+"F0.imprint","IMPRINT",EDGE,{"derivedFrom":subQ0}),1.0]])]});}
            var Q1;
            Q1=sQuery(id+"F0.wireOp",EDGE,"E33.2.7");
            revolve(context, id + "F10", {"operationType" : NewBodyOperationType.REMOVE, "surfaceOperationType" : NewSurfaceOperationType.NEW, "entities" : qUnion([Q0]), "axis" : qUnion([Q1]), "revolveType" : RevolveType.FULL, "oppositeDirection" : true});
        }
        {
            var Q0;
            {var subQ0=sQuery(id+"F0.wireOp",EDGE,"E44");var subQ1=sQuery(id+"F0.wireOp",EDGE,"E3");var subQ2=makeQuery(id+"F0.imprint","INTERSECT",VERTEX,{"derivedFrom":[subQ1,subQ0]});Q0=makeQuery(id+"F0.imprint","IMPRINT",FACE,{"disambiguationData":[TD([[makeQuery(id+"F0.imprint","IMPRINT",EDGE,{"disambiguationData":[TD([[subQ2,-1.0]])],"derivedFrom":subQ1}),-1.0]])]});}
            var Q1;
            {var subQ0=sQuery(id+"F0.wireOp",EDGE,"E45");var subQ1=sQuery(id+"F0.wireOp",EDGE,"E3");var subQ2=makeQuery(id+"F0.imprint","INTERSECT",VERTEX,{"derivedFrom":[subQ1,subQ0]});Q1=makeQuery(id+"F0.imprint","IMPRINT",FACE,{"disambiguationData":[TD([[makeQuery(id+"F0.imprint","IMPRINT",EDGE,{"disambiguationData":[TD([[subQ2,1.0]])],"derivedFrom":subQ1}),-1.0]])]});}
            var Q2;
            {var subQ0=sQuery(id+"F0.wireOp",EDGE,"E40");var subQ1=sQuery(id+"F0.wireOp",EDGE,"E3");var subQ2=makeQuery(id+"F0.imprint","INTERSECT",VERTEX,{"derivedFrom":[subQ1,subQ0]});Q2=makeQuery(id+"F0.imprint","IMPRINT",FACE,{"disambiguationData":[TD([[makeQuery(id+"F0.imprint","IMPRINT",EDGE,{"disambiguationData":[TD([[subQ2,-1.0]])],"derivedFrom":subQ1}),1.0]])]});}
            var Q3;
            {var subQ0=sQuery(id+"F0.wireOp",EDGE,"E40");var subQ1=sQuery(id+"F0.wireOp",EDGE,"E3");var subQ2=makeQuery(id+"F0.imprint","INTERSECT",VERTEX,{"derivedFrom":[subQ1,subQ0]});Q3=makeQuery(id+"F0.imprint","IMPRINT",FACE,{"disambiguationData":[TD([[makeQuery(id+"F0.imprint","IMPRINT",EDGE,{"disambiguationData":[TD([[subQ2,-1.0]])],"derivedFrom":subQ1}),-1.0]])]});}
            var Q4;
            {var subQ0=sQuery(id+"F0.wireOp",EDGE,"E37");var subQ1=sQuery(id+"F0.wireOp",EDGE,"E3");var subQ2=makeQuery(id+"F0.imprint","INTERSECT",VERTEX,{"derivedFrom":[subQ1,subQ0]});Q4=makeQuery(id+"F0.imprint","IMPRINT",FACE,{"disambiguationData":[TD([[makeQuery(id+"F0.imprint","IMPRINT",EDGE,{"disambiguationData":[TD([[subQ2,-1.0]])],"derivedFrom":subQ1}),-1.0]])]});}
            var Q5;
            {var subQ1=sQuery(id+"F0.wireOp",EDGE,"E4");var subQ6=sQuery(id+"F0.wireOp",EDGE,"E43");var subQ8=makeQuery(id+"F0.imprint","INTERSECT",VERTEX,{"derivedFrom":[subQ1,subQ6]});Q5=makeQuery(id+"F0.imprint","IMPRINT",FACE,{"disambiguationData":[TD([[makeQuery(id+"F0.imprint","IMPRINT",EDGE,{"disambiguationData":[TD([[subQ8,1.0]])],"derivedFrom":subQ1}),1.0]])]});}
            var Q6;
            {var subQ0=sQuery(id+"F0.wireOp",EDGE,"E43");var subQ1=sQuery(id+"F0.wireOp",EDGE,"E4");var subQ2=makeQuery(id+"F0.imprint","INTERSECT",VERTEX,{"derivedFrom":[subQ1,subQ0]});Q6=makeQuery(id+"F0.imprint","IMPRINT",FACE,{"disambiguationData":[TD([[makeQuery(id+"F0.imprint","IMPRINT",EDGE,{"disambiguationData":[TD([[subQ2,1.0]])],"derivedFrom":subQ1}),-1.0]])]});}
            var Q7;
            Q7=makeQuery(id+"F0.imprint","IMPRINT",FACE,{"disambiguationData":[TD([[makeQuery(id+"F0.imprint","IMPRINT",EDGE,{"derivedFrom":sQuery(id+"F0.wireOp",EDGE,"E2")}),1.0]])]});
            var Q8;
            {var subQ0=sQuery(id+"F0.wireOp",EDGE,"E37");var subQ1=sQuery(id+"F0.wireOp",EDGE,"E4");var subQ2=makeQuery(id+"F0.imprint","INTERSECT",VERTEX,{"derivedFrom":[subQ1,subQ0]});Q8=makeQuery(id+"F0.imprint","IMPRINT",FACE,{"disambiguationData":[TD([[makeQuery(id+"F0.imprint","IMPRINT",EDGE,{"disambiguationData":[TD([[subQ2,-1.0]])],"derivedFrom":subQ1}),-1.0]])]});}
            var Q9;
            {var subQ0=sQuery(id+"F0.wireOp",EDGE,"E37");var subQ1=sQuery(id+"F0.wireOp",EDGE,"E4");var subQ2=makeQuery(id+"F0.imprint","INTERSECT",VERTEX,{"derivedFrom":[subQ1,subQ0]});Q9=makeQuery(id+"F0.imprint","IMPRINT",FACE,{"disambiguationData":[TD([[makeQuery(id+"F0.imprint","IMPRINT",EDGE,{"disambiguationData":[TD([[subQ2,-1.0]])],"derivedFrom":subQ1}),1.0]])]});}
            var Q10;
            {var subQ5=sQuery(id+"F0.wireOp",EDGE,"E46");Q10=makeQuery(id+"F0.imprint","IMPRINT",FACE,{"disambiguationData":[TD([[makeQuery(id+"F0.imprint","IMPRINT",EDGE,{"derivedFrom":subQ5}),1.0]])]});}
            var Q11;
            {var subQ5=sQuery(id+"F0.wireOp",EDGE,"E38");Q11=makeQuery(id+"F0.imprint","IMPRINT",FACE,{"disambiguationData":[TD([[makeQuery(id+"F0.imprint","IMPRINT",EDGE,{"derivedFrom":subQ5}),-1.0]])]});}
            var Q12;
            {var subQ0=sQuery(id+"F0.wireOp",EDGE,"E44");var subQ1=sQuery(id+"F0.wireOp",EDGE,"E3");var subQ2=makeQuery(id+"F0.imprint","INTERSECT",VERTEX,{"derivedFrom":[subQ1,subQ0]});Q12=makeQuery(id+"F0.imprint","IMPRINT",FACE,{"disambiguationData":[TD([[makeQuery(id+"F0.imprint","IMPRINT",EDGE,{"disambiguationData":[TD([[subQ2,-1.0]])],"derivedFrom":subQ1}),1.0]])]});}
            extrude(context, id + "F11", {"entities" : qUnion([Q0, Q1, Q2, Q3, Q4, Q5, Q6, Q7, Q8, Q9, Q10, Q11, Q12]), "depth" : 3 * mm, "offsetDistance" : 25 * mm});
        }
        {
            var Q0;
            {var subQ6=sQuery(id+"F0.wireOp",EDGE,"E38");Q0=makeQuery(id+"F0.imprint","IMPRINT",FACE,{"disambiguationData":[TD([[makeQuery(id+"F0.imprint","IMPRINT",EDGE,{"derivedFrom":subQ6}),1.0]])]});}
            var Q1;
            {var subQ5=sQuery(id+"F0.wireOp",EDGE,"E46");Q1=makeQuery(id+"F0.imprint","IMPRINT",FACE,{"disambiguationData":[TD([[makeQuery(id+"F0.imprint","IMPRINT",EDGE,{"derivedFrom":subQ5}),1.0]])]});}
            var Q2;
            {var subQ5=sQuery(id+"F0.wireOp",EDGE,"E38");Q2=makeQuery(id+"F0.imprint","IMPRINT",FACE,{"disambiguationData":[TD([[makeQuery(id+"F0.imprint","IMPRINT",EDGE,{"derivedFrom":subQ5}),-1.0]])]});}
            var Q3;
            {var subQ0=sQuery(id+"F0.wireOp",EDGE,"E40");var subQ1=sQuery(id+"F0.wireOp",EDGE,"E3");var subQ2=makeQuery(id+"F0.imprint","INTERSECT",VERTEX,{"derivedFrom":[subQ1,subQ0]});Q3=makeQuery(id+"F0.imprint","IMPRINT",FACE,{"disambiguationData":[TD([[makeQuery(id+"F0.imprint","IMPRINT",EDGE,{"disambiguationData":[TD([[subQ2,-1.0]])],"derivedFrom":subQ1}),1.0]])]});}
            var Q4;
            {var subQ0=sQuery(id+"F0.wireOp",EDGE,"E44");var subQ1=sQuery(id+"F0.wireOp",EDGE,"E3");var subQ2=makeQuery(id+"F0.imprint","INTERSECT",VERTEX,{"derivedFrom":[subQ1,subQ0]});Q4=makeQuery(id+"F0.imprint","IMPRINT",FACE,{"disambiguationData":[TD([[makeQuery(id+"F0.imprint","IMPRINT",EDGE,{"disambiguationData":[TD([[subQ2,-1.0]])],"derivedFrom":subQ1}),1.0]])]});}
            extrude(context, id + "F12", {"entities" : qUnion([Q0, Q1, Q2, Q3, Q4]), "operationType" : NewBodyOperationType.ADD, "depth" : 7 * mm, "offsetDistance" : 25 * mm, "hasSecondDirection" : true, "secondDirectionOppositeDirection" : false, "secondDirectionDepth" : 0.5 * mm});
        }
        {
            var Q0;
            {var subQ0=sQuery(id+"F0.wireOp",EDGE,"E44");var subQ1=sQuery(id+"F0.wireOp",EDGE,"E3");var subQ2=makeQuery(id+"F0.imprint","INTERSECT",VERTEX,{"derivedFrom":[subQ1,subQ0]});Q0=makeQuery(id+"F0.imprint","IMPRINT",FACE,{"disambiguationData":[TD([[makeQuery(id+"F0.imprint","IMPRINT",EDGE,{"disambiguationData":[TD([[subQ2,1.0]])],"derivedFrom":subQ1}),-1.0]])]});}
            var Q1;
            {var subQ0=sQuery(id+"F0.wireOp",EDGE,"E39");var subQ1=sQuery(id+"F0.wireOp",EDGE,"E3");var subQ2=makeQuery(id+"F0.imprint","INTERSECT",VERTEX,{"derivedFrom":[subQ1,subQ0]});Q1=makeQuery(id+"F0.imprint","IMPRINT",FACE,{"disambiguationData":[TD([[makeQuery(id+"F0.imprint","IMPRINT",EDGE,{"disambiguationData":[TD([[subQ2,-1.0]])],"derivedFrom":subQ1}),-1.0]])]});}
            var Q2;
            {var subQ0=sQuery(id+"F0.wireOp",EDGE,"E37");var subQ1=sQuery(id+"F0.wireOp",EDGE,"E3");var subQ2=makeQuery(id+"F0.imprint","INTERSECT",VERTEX,{"derivedFrom":[subQ1,subQ0]});Q2=makeQuery(id+"F0.imprint","IMPRINT",FACE,{"disambiguationData":[TD([[makeQuery(id+"F0.imprint","IMPRINT",EDGE,{"disambiguationData":[TD([[subQ2,-1.0]])],"derivedFrom":subQ1}),-1.0]])]});}
            var Q3;
            {var subQ0=sQuery(id+"F0.wireOp",EDGE,"E40");var subQ1=sQuery(id+"F0.wireOp",EDGE,"E3");var subQ2=makeQuery(id+"F0.imprint","INTERSECT",VERTEX,{"derivedFrom":[subQ1,subQ0]});Q3=makeQuery(id+"F0.imprint","IMPRINT",FACE,{"disambiguationData":[TD([[makeQuery(id+"F0.imprint","IMPRINT",EDGE,{"disambiguationData":[TD([[subQ2,-1.0]])],"derivedFrom":subQ1}),-1.0]])]});}
            var Q4;
            {var subQ0=sQuery(id+"F0.wireOp",EDGE,"E45");var subQ1=sQuery(id+"F0.wireOp",EDGE,"E3");var subQ2=makeQuery(id+"F0.imprint","INTERSECT",VERTEX,{"derivedFrom":[subQ1,subQ0]});Q4=makeQuery(id+"F0.imprint","IMPRINT",FACE,{"disambiguationData":[TD([[makeQuery(id+"F0.imprint","IMPRINT",EDGE,{"disambiguationData":[TD([[subQ2,1.0]])],"derivedFrom":subQ1}),-1.0]])]});}
            var Q5;
            {var subQ0=sQuery(id+"F0.wireOp",EDGE,"E41");var subQ1=sQuery(id+"F0.wireOp",EDGE,"E3");var subQ2=makeQuery(id+"F0.imprint","INTERSECT",VERTEX,{"derivedFrom":[subQ1,subQ0]});Q5=makeQuery(id+"F0.imprint","IMPRINT",FACE,{"disambiguationData":[TD([[makeQuery(id+"F0.imprint","IMPRINT",EDGE,{"disambiguationData":[TD([[subQ2,-1.0]])],"derivedFrom":subQ1}),-1.0]])]});}
            var Q6;
            {var subQ0=sQuery(id+"F0.wireOp",EDGE,"E43");var subQ1=sQuery(id+"F0.wireOp",EDGE,"E3");var subQ2=makeQuery(id+"F0.imprint","INTERSECT",VERTEX,{"derivedFrom":[subQ1,subQ0]});Q6=makeQuery(id+"F0.imprint","IMPRINT",FACE,{"disambiguationData":[TD([[makeQuery(id+"F0.imprint","IMPRINT",EDGE,{"disambiguationData":[TD([[subQ2,-1.0]])],"derivedFrom":subQ1}),-1.0]])]});}
            var Q7;
            {var subQ0=sQuery(id+"F0.wireOp",EDGE,"E44");var subQ1=sQuery(id+"F0.wireOp",EDGE,"E3");var subQ2=makeQuery(id+"F0.imprint","INTERSECT",VERTEX,{"derivedFrom":[subQ1,subQ0]});Q7=makeQuery(id+"F0.imprint","IMPRINT",FACE,{"disambiguationData":[TD([[makeQuery(id+"F0.imprint","IMPRINT",EDGE,{"disambiguationData":[TD([[subQ2,-1.0]])],"derivedFrom":subQ1}),-1.0]])]});}
            extrude(context, id + "F13", {"entities" : qUnion([Q0, Q1, Q2, Q3, Q4, Q5, Q6, Q7]), "operationType" : NewBodyOperationType.ADD, "depth" : 4 * mm, "offsetDistance" : 25 * mm, "hasSecondDirection" : true, "secondDirectionOppositeDirection" : false, "secondDirectionDepth" : 0.5 * mm});
        }
        {
            var Q0;
            {var subQ0=sQuery(id+"F0.wireOp",EDGE,"E41");var subQ1=sQuery(id+"F0.wireOp",EDGE,"E4");var subQ2=makeQuery(id+"F0.imprint","INTERSECT",VERTEX,{"derivedFrom":[subQ1,subQ0]});Q0=makeQuery(id+"F0.imprint","IMPRINT",FACE,{"disambiguationData":[TD([[makeQuery(id+"F0.imprint","IMPRINT",EDGE,{"disambiguationData":[TD([[subQ2,-1.0]])],"derivedFrom":subQ1}),1.0]])]});}
            var Q1;
            {var subQ0=sQuery(id+"F0.wireOp",EDGE,"E41");var subQ1=sQuery(id+"F0.wireOp",EDGE,"E4");var subQ2=makeQuery(id+"F0.imprint","INTERSECT",VERTEX,{"derivedFrom":[subQ1,subQ0]});Q1=makeQuery(id+"F0.imprint","IMPRINT",FACE,{"disambiguationData":[TD([[makeQuery(id+"F0.imprint","IMPRINT",EDGE,{"disambiguationData":[TD([[subQ2,-1.0]])],"derivedFrom":subQ1}),-1.0]])]});}
            var Q2;
            {var subQ0=sQuery(id+"F0.wireOp",EDGE,"E37");var subQ1=sQuery(id+"F0.wireOp",EDGE,"E4");var subQ2=makeQuery(id+"F0.imprint","INTERSECT",VERTEX,{"derivedFrom":[subQ1,subQ0]});Q2=makeQuery(id+"F0.imprint","IMPRINT",FACE,{"disambiguationData":[TD([[makeQuery(id+"F0.imprint","IMPRINT",EDGE,{"disambiguationData":[TD([[subQ2,1.0]])],"derivedFrom":subQ1}),1.0]])]});}
            var Q3;
            {var subQ0=sQuery(id+"F0.wireOp",EDGE,"E37");var subQ1=sQuery(id+"F0.wireOp",EDGE,"E4");var subQ2=makeQuery(id+"F0.imprint","INTERSECT",VERTEX,{"derivedFrom":[subQ1,subQ0]});Q3=makeQuery(id+"F0.imprint","IMPRINT",FACE,{"disambiguationData":[TD([[makeQuery(id+"F0.imprint","IMPRINT",EDGE,{"disambiguationData":[TD([[subQ2,1.0]])],"derivedFrom":subQ1}),-1.0]])]});}
            extrude(context, id + "F14", {"entities" : qUnion([Q0, Q1, Q2, Q3]), "operationType" : NewBodyOperationType.ADD, "depth" : 3 * mm, "offsetDistance" : 25 * mm, "hasSecondDirection" : true, "secondDirectionOppositeDirection" : false, "secondDirectionDepth" : 0.5 * mm});
        }
        {
            var Q0;
            Q0=makeQuery(id+"F11.opExtrude","CAP_EDGE",EDGE,{"disambiguationData":[OSD([sQuery(id+"F0.wireOp",EDGE,"E2")])],"isStart":true});
            fillet(context, id + "F15", {"entities" : qUnion([Q0]), "radius" : 2 * mm, "tangentPropagation" : true, "allowEdgeOverflow" : false});
        }
        {
            var Q0;
            Q0=makeQuery(id+"F11.opExtrude","SWEPT_BODY",BODY,{"disambiguationData":[OSD([sQuery(id+"F0.wireOp",EDGE,"E2"),sQuery(id+"F0.wireOp",EDGE,"E37"),sQuery(id+"F0.wireOp",EDGE,"E38"),sQuery(id+"F0.wireOp",EDGE,"E39"),sQuery(id+"F0.wireOp",EDGE,"E40"),sQuery(id+"F0.wireOp",EDGE,"E41"),sQuery(id+"F0.wireOp",EDGE,"E42"),sQuery(id+"F0.wireOp",EDGE,"E43"),sQuery(id+"F0.wireOp",EDGE,"E44"),sQuery(id+"F0.wireOp",EDGE,"E45"),sQuery(id+"F0.wireOp",EDGE,"E46")])]});
            var Q1;
            Q1=qCreatedBy(makeId("Top.planeOp"),FACE);
            mirror(context, id + "F16", {"entities" : qUnion([Q0]), "mirrorPlane" : qUnion([Q1])});
        }
    });
